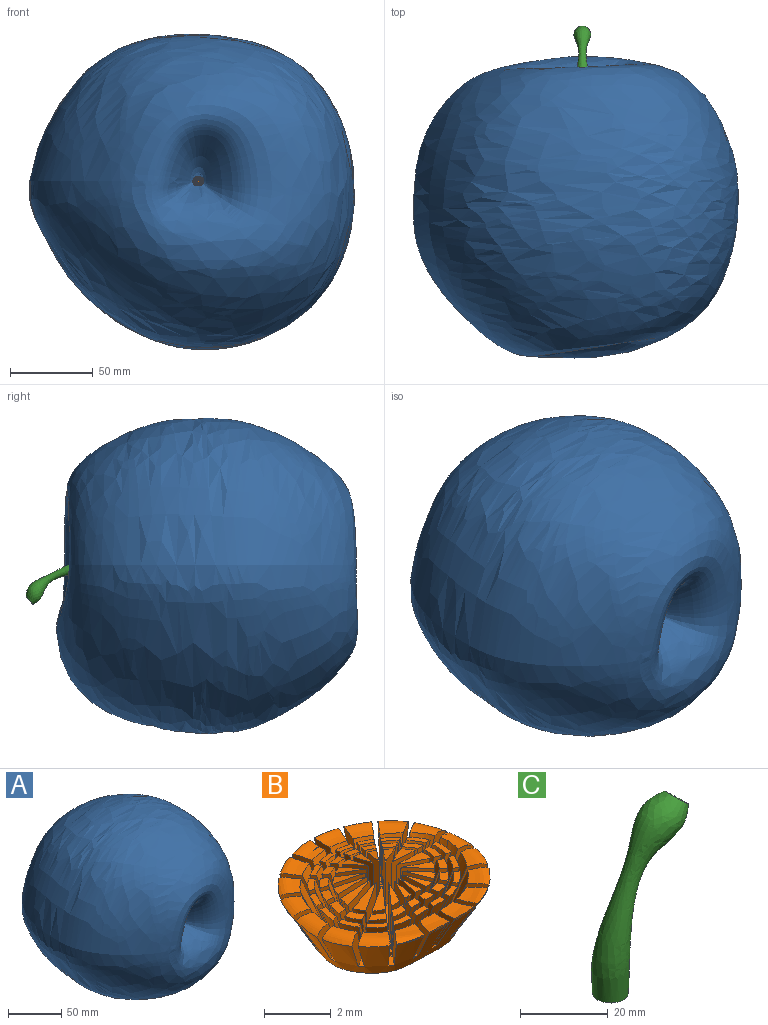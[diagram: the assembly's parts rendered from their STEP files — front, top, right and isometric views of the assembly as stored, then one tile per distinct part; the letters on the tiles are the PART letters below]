
ASSEMBLY  parts=3 mates=2
PART A: 3 faces, bbox 196.9x182.4x190.9 mm
  f0: plane 5.17x4.24mm, normal (0,-1,0), area 15.4mm2, adj f2
  f1: plane 5.17x4.24mm, normal (0,1,0), area 15.4mm2, adj f2
  f2: bspline ~196.63x190.63mm, area 122945.4mm2, adj f0,f1
PART B: 333 faces, bbox 7.9x6.9x3.2 mm
  f0: plane 0.16x0.05mm, normal (0,0,1), area 0mm2, adj f23,f253,f268
  f1: plane 0.15x0.1mm, normal (0,0,1), area 0mm2, adj f22,f260,f261
  f2: plane 0.15x0.1mm, normal (0,0,1), area 0mm2, adj f27,f245,f276
  f3: plane 0.13x0.12mm, normal (0,0,1), area 0mm2, adj f26,f252,f269
  f4: plane 0.13x0.12mm, normal (0,0,1), area 0mm2, adj f30,f237,f284
  f5: plane 0.15x0.08mm, normal (0,0,1), area 0mm2, adj f29,f244,f277
  f6: plane 0.15x0.08mm, normal (0,0,1), area 0mm2, adj f32,f229,f292
  f7: plane 0.15x0.05mm, normal (0,0,1), area 0mm2, adj f31,f236,f285
  f8: plane 0.15x0.05mm, normal (0,0,1), area 0mm2, adj f35,f221,f300
  f9: plane 0.15x0.08mm, normal (0,0,1), area 0mm2, adj f34,f228,f293
  f10: plane 0.15x0.08mm, normal (0,0,1), area 0mm2, adj f39,f213,f308
  f11: plane 0.13x0.12mm, normal (0,0,1), area 0mm2, adj f38,f220,f301
  f12: plane 0.13x0.12mm, normal (0,0,1), area 0mm2, adj f43,f205,f316
  f13: plane 0.15x0.1mm, normal (0,0,1), area 0mm2, adj f42,f212,f309
  f14: plane 0.15x0.1mm, normal (0,0,1), area 0mm2, adj f47,f197,f324
  f15: plane 0.16x0.05mm, normal (0,0,1), area 0mm2, adj f46,f204,f317
  f16: plane 0.16x0.05mm, normal (0,0,1), area 0mm2, adj f50,f190,f328
  f17: plane 0.16x0.05mm, normal (0,0,1), area 0mm2, adj f51,f177,f332
  f18: bspline ~2.16x0.71mm, area 0.1mm2, adj f75,f259,f262
  f19: bspline ~0.87x0.23mm, area 0.1mm2, adj f76,f253,f268
  f20: bspline ~1.79x1.22mm, area 0.1mm2, adj f53,f176,f254,f267
  f21: bspline ~1.67x0.54mm, area 0.1mm2, adj f49,f54,f255,f266
  f22: plane 1.67x0.7mm, normal (0.77,-0.64,0), area 1.1mm2, adj f1,f74,f80,f260,f261
  f23: plane 1.67x0.73mm, normal (1,0,0), area 0.8mm2, adj f0,f76,f80,f253,f268
  f24: bspline ~1.83x1.04mm, area 0.1mm2, adj f54,f186,f247,f274
  f25: bspline ~1.95x1.66mm, area 0mm2, adj f53,f163,f246,f275
  f26: plane 1.68x0.9mm, normal (0.5,-0.87,0), area 1.3mm2, adj f3,f74,f80,f252,f269
  f27: plane 1.67x0.78mm, normal (0.94,-0.34,0), area 1mm2, adj f2,f79,f80,f245,f276
  f28: bspline ~0.84x0.77mm, area 0mm2, adj f54,f173,f282
  f29: plane 1.69x1.26mm, normal (0.17,-0.98,0), area 1.6mm2, adj f5,f74,f80,f244,f277
  f30: plane 1.68x0.84mm, normal (0.77,-0.64,0), area 1.3mm2, adj f4,f79,f80,f237,f284
  f31: plane 1.69x1.25mm, normal (-0.17,-0.98,0), area 1.6mm2, adj f7,f76,f80,f236,f285
  f32: plane 1.69x1.07mm, normal (0.5,-0.87,0), area 1.6mm2, adj f6,f79,f80,f229,f292
  f33: bspline ~0.64x0.63mm, area 0mm2, adj f55,f125,f298
  f34: plane 1.69x0.96mm, normal (-0.5,-0.87,0), area 1.4mm2, adj f9,f76,f80,f228,f293
  f35: plane 1.69x1.23mm, normal (0.17,-0.98,0), area 1.6mm2, adj f8,f79,f80,f221,f300
  f36: bspline ~2.43x1.36mm, area 0mm2, adj f53,f214,f307
  f37: bspline ~1.58x1.45mm, area 0mm2, adj f55,f113,f215,f306
  f38: plane 1.68x0.77mm, normal (-0.77,-0.64,0), area 1.2mm2, adj f11,f76,f80,f220,f301
  f39: plane 1.69x1.1mm, normal (-0.17,-0.98,0), area 1.4mm2, adj f10,f74,f80,f213,f308
  f40: bspline ~1.64x1.62mm, area 0mm2, adj f53,f128,f206,f315
  f41: bspline ~1.89x1.15mm, area 0.1mm2, adj f55,f101,f207,f314
  f42: plane 1.67x0.8mm, normal (-0.94,-0.34,0), area 1mm2, adj f13,f76,f80,f212,f309
  f43: plane 1.68x0.91mm, normal (-0.5,-0.87,0), area 1.3mm2, adj f12,f74,f80,f205,f316
  f44: bspline ~1.92x1.22mm, area 0.1mm2, adj f53,f115,f198,f323
  f45: bspline ~1.91x0.6mm, area 0.1mm2, adj f55,f89,f199,f322
  f46: plane 1.67x0.74mm, normal (-1,0,0), area 0.9mm2, adj f15,f76,f80,f204,f317
  f47: plane 1.68x0.74mm, normal (-0.77,-0.64,0), area 1.2mm2, adj f14,f74,f80,f197,f324
  f48: bspline ~2.16x0.74mm, area 0.1mm2, adj f53,f104,f191,f327
  f49: bspline ~1.3x0.48mm, area 0mm2, adj f21,f55,f192,f266
  f50: plane 1.67x0.86mm, normal (-0.94,-0.34,0), area 1.1mm2, adj f16,f74,f80,f190,f328
  f51: plane 1.67x0.88mm, normal (-1,0,0), area 1.1mm2, adj f17,f74,f80,f177,f332
  f52: bspline ~2.31x0.97mm, area 0.1mm2, adj f53,f92,f188,f329
  f53: bspline ~7.64x3.37mm, area 12.9mm2, adj f20,f25,f36,f40,f44,f48,f52,f54
  f54: bspline ~3.77x3.61mm, area 6.9mm2, adj f21,f24,f28,f53,f55,f56,f149,f150
  f55: bspline ~4.21x3.53mm, area 7.2mm2, adj f33,f37,f41,f45,f49,f53,f54,f56
  f56: plane 4.92x3.99mm, normal (0,0,-1), area 15.4mm2, adj f53,f54,f55
  f57: bspline ~5.01x2.2mm, area 7.3mm2, adj f58,f60,f63,f87,f88,f99,f100,f111
  f58: bspline ~4.2x1.8mm, area 0.9mm2, adj f57,f59,f61,f64
  f59: bspline ~5.49x2.42mm, area 8.7mm2, adj f58,f62,f65,f91,f92,f103,f104,f115
  f60: bspline ~3.4x2.79mm, area 4.1mm2, adj f57,f61,f63,f85,f86,f97,f98,f109
  f61: bspline ~2.52x1.58mm, area 0.5mm2, adj f58,f60,f62,f64
  f62: bspline ~3.51x2.78mm, area 4.9mm2, adj f59,f61,f65,f89,f90,f101,f102,f113
  f63: bspline ~2.79x2.79mm, area 3.9mm2, adj f57,f60,f64,f147,f148,f159,f160,f171
  f64: bspline ~1.79x1.74mm, area 0.4mm2, adj f58,f61,f63,f65
  f65: bspline ~2.94x2.81mm, area 4.7mm2, adj f59,f62,f64,f149,f150,f161,f162,f173
  f66: bspline ~2.09x1.91mm, area 3.3mm2, adj f68,f70,f71,f147,f148,f159,f160,f171
  f67: bspline ~1.9x1.74mm, area 3mm2, adj f69,f71,f72,f141,f142,f153,f154,f165
  f68: bspline ~5.06x2.19mm, area 6.5mm2, adj f66,f70,f71,f87,f88,f99,f100,f111
  f69: bspline ~4.83x2.38mm, area 5.9mm2, adj f67,f71,f72,f83,f84,f95,f96,f107
  f70: bspline ~2.72x1.91mm, area 3.7mm2, adj f66,f68,f71,f85,f86,f97,f98,f109
  f71: plane 3.83x2.88mm, normal (0,0,1), area 1.1mm2, adj f66,f67,f68,f69,f70,f72
  f72: bspline ~2.58x1.72mm, area 3.4mm2, adj f67,f69,f71,f81,f82,f93,f94,f105
  f73: bspline ~3.84x1.56mm, area 4.6mm2, adj f75,f77,f78,f83,f84,f95,f96,f107
  f74: bspline ~3.54x1.59mm, area 4.2mm2, adj f22,f26,f29,f39,f43,f47,f50,f51
  f75: bspline ~2.29x1.58mm, area 2.6mm2, adj f18,f73,f77,f78,f81,f82,f93,f94
  f76: bspline ~2.16x1.61mm, area 2.4mm2, adj f19,f23,f31,f34,f38,f42,f46,f74
  f77: bspline ~1.7x1.56mm, area 2mm2, adj f73,f75,f78,f141,f142,f153,f154,f165
  f78: plane 3x2.02mm, normal (0,0,1), area 0.3mm2, adj f73,f74,f75,f76,f77,f79
  f79: bspline ~2.28x1.74mm, area 1.9mm2, adj f27,f30,f32,f35,f74,f76,f78,f80
  f80: plane 2.93x1.98mm, normal (0,0,1), area 3mm2, adj f22,f23,f26,f27,f29,f30,f31,f32
  f81: plane 1.48x0.73mm, normal (-1,0,0), area 0.4mm2, adj f72,f75,f82,f318
  f82: plane 0.32x0.2mm, normal (0,0,1), area 0.1mm2, adj f72,f75,f81,f196
  f83: plane 1.46x0.73mm, normal (-1,0,0), area 0.4mm2, adj f69,f73,f84,f331
  f84: plane 0.32x0.19mm, normal (0,0,1), area 0.1mm2, adj f69,f73,f83,f195
  f85: plane 1.4x0.65mm, normal (-1,0,0), area 0.2mm2, adj f60,f70,f86,f320
  f86: plane 0.2x0.16mm, normal (0,0,1), area 0mm2, adj f60,f70,f85,f194
  f87: plane 1.39x0.65mm, normal (-1,0,0), area 0.2mm2, adj f57,f68,f88,f330
  f88: plane 0.19x0.16mm, normal (0,0,1), area 0mm2, adj f57,f68,f87,f193
  f89: plane 1.48x1.34mm, normal (-1,0,0), area 0.8mm2, adj f45,f55,f62,f90,f322
  f90: plane 0.47x0.19mm, normal (0,0,1), area 0.1mm2, adj f55,f62,f89,f192
  f91: plane 0.46x0.19mm, normal (0,0,1), area 0.1mm2, adj f53,f59,f92,f191
  f92: plane 1.48x1.34mm, normal (-1,0,0), area 0.8mm2, adj f52,f53,f59,f91,f329
  f93: plane 1.46x0.7mm, normal (-0.94,-0.34,0), area 0.4mm2, adj f72,f75,f94,f310
  f94: plane 0.33x0.33mm, normal (0,0,1), area 0.1mm2, adj f72,f75,f93,f203
  f95: plane 1.45x0.68mm, normal (-0.94,-0.34,0), area 0.4mm2, adj f69,f73,f96,f325
  f96: plane 0.34x0.29mm, normal (0,0,1), area 0.1mm2, adj f69,f73,f95,f202
  f97: plane 1.39x0.62mm, normal (-0.94,-0.34,0), area 0.2mm2, adj f60,f70,f98,f312
  f98: plane 0.26x0.17mm, normal (0,0,1), area 0mm2, adj f60,f70,f97,f201
  f99: plane 1.38x0.61mm, normal (-0.94,-0.34,0), area 0.2mm2, adj f57,f68,f100,f326
  f100: plane 0.24x0.19mm, normal (0,0,1), area 0mm2, adj f57,f68,f99,f200
  f101: plane 1.48x1.28mm, normal (-0.94,-0.34,0), area 0.8mm2, adj f41,f55,f62,f102,f314
  f102: plane 0.47x0.36mm, normal (0,0,1), area 0.1mm2, adj f55,f62,f101,f199
  f103: plane 0.49x0.34mm, normal (0,0,1), area 0.1mm2, adj f53,f59,f104,f198
  f104: plane 1.48x1.26mm, normal (-0.94,-0.34,0), area 0.8mm2, adj f48,f53,f59,f103,f327
  f105: plane 1.44x0.56mm, normal (-0.77,-0.64,0), area 0.4mm2, adj f72,f75,f106,f302
  f106: plane 0.4x0.34mm, normal (0,0,1), area 0.1mm2, adj f72,f75,f105,f211
  f107: plane 1.44x0.56mm, normal (-0.77,-0.64,0), area 0.4mm2, adj f69,f73,f108,f319
  f108: plane 0.37x0.34mm, normal (0,0,1), area 0.1mm2, adj f69,f73,f107,f210
  f109: plane 1.37x0.5mm, normal (-0.77,-0.64,0), area 0.2mm2, adj f60,f70,f110,f304
  f110: plane 0.27x0.22mm, normal (0,0,1), area 0mm2, adj f60,f70,f109,f209
  f111: plane 1.37x0.5mm, normal (-0.77,-0.64,0), area 0.2mm2, adj f57,f68,f112,f321
  f112: plane 0.26x0.22mm, normal (0,0,1), area 0mm2, adj f57,f68,f111,f208
  f113: plane 1.45x1.02mm, normal (-0.77,-0.64,0), area 0.8mm2, adj f37,f55,f62,f114,f306
  f114: plane 0.47x0.46mm, normal (0,0,1), area 0.1mm2, adj f55,f62,f113,f207
  f115: plane 1.46x1.03mm, normal (-0.77,-0.64,0), area 0.8mm2, adj f44,f53,f59,f116,f323
  f116: plane 0.46x0.46mm, normal (0,0,1), area 0.1mm2, adj f53,f59,f115,f206
  f117: plane 1.42x0.62mm, normal (-0.5,-0.87,0), area 0.4mm2, adj f72,f75,f118,f294
  f118: plane 0.41x0.3mm, normal (0,0,1), area 0.1mm2, adj f72,f75,f117,f219
  f119: plane 1.43x0.63mm, normal (-0.5,-0.87,0), area 0.4mm2, adj f69,f73,f120,f311
  f120: plane 0.4x0.31mm, normal (0,0,1), area 0.1mm2, adj f69,f73,f119,f218
  f121: plane 1.36x0.56mm, normal (-0.5,-0.87,0), area 0.2mm2, adj f60,f70,f122,f296
  f122: plane 0.26x0.22mm, normal (0,0,1), area 0mm2, adj f60,f70,f121,f217
  f123: plane 1.36x0.56mm, normal (-0.5,-0.87,0), area 0.2mm2, adj f57,f68,f124,f313
  f124: plane 0.25x0.23mm, normal (0,0,1), area 0mm2, adj f57,f68,f123,f216
  f125: plane 1.37x1.05mm, normal (-0.5,-0.87,0), area 0.8mm2, adj f33,f55,f62,f126,f298
  f126: plane 0.53x0.38mm, normal (0,0,1), area 0.1mm2, adj f55,f62,f125,f215
  f127: plane 0.51x0.39mm, normal (0,0,1), area 0.1mm2, adj f53,f59,f128,f214
  f128: plane 1.43x1.12mm, normal (-0.5,-0.87,0), area 0.8mm2, adj f40,f53,f59,f127,f315
  f129: plane 1.39x0.71mm, normal (-0.17,-0.98,0), area 0.4mm2, adj f72,f75,f130,f287
  f130: plane 0.42x0.24mm, normal (0,0,1), area 0.1mm2, adj f72,f75,f129,f227
  f131: plane 1.41x0.71mm, normal (-0.17,-0.98,0), area 0.4mm2, adj f69,f73,f132,f303
  f132: plane 0.38x0.24mm, normal (0,0,1), area 0.1mm2, adj f69,f73,f131,f226
  f133: plane 1.35x0.63mm, normal (-0.17,-0.98,0), area 0.2mm2, adj f60,f70,f134,f288
  f134: plane 0.24x0.21mm, normal (0,0,1), area 0mm2, adj f60,f70,f133,f225
  f135: plane 1.36x0.64mm, normal (-0.17,-0.98,0), area 0.2mm2, adj f57,f68,f136,f305
  f136: plane 0.21x0.21mm, normal (0,0,1), area 0mm2, adj f57,f68,f135,f224
  f137: plane 1.4x1.16mm, normal (-0.17,-0.98,0), area 0.7mm2, adj f55,f62,f138,f291
  f138: plane 0.53x0.26mm, normal (0,0,1), area 0.1mm2, adj f55,f62,f137,f223
  f139: plane 1.4x1.22mm, normal (-0.17,-0.98,0), area 0.8mm2, adj f53,f59,f140,f307
  f140: plane 0.51x0.27mm, normal (0,0,1), area 0.1mm2, adj f53,f59,f139,f222
  f141: plane 1.4x0.73mm, normal (0.17,-0.98,0), area 0.4mm2, adj f67,f77,f142,f295
  f142: plane 0.39x0.3mm, normal (0,0,1), area 0.1mm2, adj f67,f77,f141,f235
  f143: plane 1.41x0.77mm, normal (0.17,-0.98,0), area 0.4mm2, adj f69,f73,f144,f279
  f144: plane 0.45x0.25mm, normal (0,0,1), area 0.1mm2, adj f69,f73,f143,f234
  f145: plane 1.38x0.68mm, normal (0.17,-0.98,0), area 0.2mm2, adj f57,f68,f146,f280
  f146: plane 0.23x0.22mm, normal (0,0,1), area 0mm2, adj f57,f68,f145,f233
  f147: plane 1.35x0.64mm, normal (0.17,-0.98,0), area 0.2mm2, adj f63,f66,f148,f297
  f148: plane 0.24x0.18mm, normal (0,0,1), area 0mm2, adj f63,f66,f147,f232
  f149: plane 1.4x1.17mm, normal (0.17,-0.98,0), area 0.7mm2, adj f54,f65,f150,f299
  f150: plane 0.47x0.28mm, normal (0,0,1), area 0.1mm2, adj f54,f65,f149,f231
  f151: plane 0.52x0.27mm, normal (0,0,1), area 0.1mm2, adj f53,f59,f152,f230
  f152: plane 1.41x1.17mm, normal (0.17,-0.98,0), area 0.8mm2, adj f53,f59,f151,f283
  f153: plane 1.42x0.64mm, normal (0.5,-0.87,0), area 0.4mm2, adj f67,f77,f154,f286
  f154: plane 0.43x0.34mm, normal (0,0,1), area 0.1mm2, adj f67,f77,f153,f243
  f155: plane 1.44x0.68mm, normal (0.5,-0.87,0), area 0.4mm2, adj f69,f73,f156,f271
  f156: plane 0.45x0.29mm, normal (0,0,1), area 0.1mm2, adj f69,f73,f155,f242
  f157: plane 1.38x0.6mm, normal (0.5,-0.87,0), area 0.2mm2, adj f57,f68,f158,f272
  f158: plane 0.29x0.21mm, normal (0,0,1), area 0mm2, adj f57,f68,f157,f241
  f159: plane 1.36x0.57mm, normal (0.5,-0.87,0), area 0.2mm2, adj f63,f66,f160,f289
  f160: plane 0.25x0.23mm, normal (0,0,1), area 0mm2, adj f63,f66,f159,f240
  f161: plane 1.39x1.03mm, normal (0.5,-0.87,0), area 0.7mm2, adj f54,f65,f162,f290
  f162: plane 0.52x0.38mm, normal (0,0,1), area 0.1mm2, adj f54,f65,f161,f239
  f163: plane 1.42x1.14mm, normal (0.5,-0.87,0), area 0.8mm2, adj f25,f53,f59,f164,f275
  f164: plane 0.56x0.38mm, normal (0,0,1), area 0.1mm2, adj f53,f59,f163,f238
  f165: plane 1.45x0.61mm, normal (0.77,-0.64,0), area 0.4mm2, adj f67,f77,f166,f278
  f166: plane 0.48x0.34mm, normal (0,0,1), area 0.1mm2, adj f67,f77,f165,f251
  f167: plane 1.47x0.58mm, normal (0.77,-0.64,0), area 0.4mm2, adj f69,f73,f168,f263
  f168: plane 0.37x0.34mm, normal (0,0,1), area 0.1mm2, adj f69,f73,f167,f250
  f169: plane 1.39x0.51mm, normal (0.77,-0.64,0), area 0.2mm2, adj f57,f68,f170,f264
  f170: plane 0.26x0.21mm, normal (0,0,1), area 0mm2, adj f57,f68,f169,f249
  f171: plane 1.39x0.54mm, normal (0.77,-0.64,0), area 0.2mm2, adj f63,f66,f172,f281
  f172: plane 0.32x0.2mm, normal (0,0,1), area 0mm2, adj f63,f66,f171,f248
  f173: plane 1.41x0.97mm, normal (0.77,-0.64,0), area 0.8mm2, adj f28,f54,f65,f174,f282
  f174: plane 0.49x0.45mm, normal (0,0,1), area 0.1mm2, adj f54,f65,f173,f247
  f175: plane 0.46x0.46mm, normal (0,0,1), area 0.1mm2, adj f53,f59,f176,f246
  f176: plane 1.48x1.06mm, normal (0.77,-0.64,0), area 0.8mm2, adj f20,f53,f59,f175,f267
  f177: plane 1.67x0.82mm, normal (0.94,-0.34,0), area 1.1mm2, adj f17,f51,f74,f80,f332
  f178: plane 1.47x0.73mm, normal (0.94,-0.34,0), area 0.4mm2, adj f67,f77,f179,f270
  f179: plane 0.32x0.31mm, normal (0,0,1), area 0.1mm2, adj f67,f75,f77,f178,f259
  f180: plane 1.48x0.69mm, normal (0.94,-0.34,0), area 0.4mm2, adj f69,f73,f181,f331
  f181: plane 0.36x0.29mm, normal (0,0,1), area 0.1mm2, adj f69,f73,f180,f258
  f182: plane 1.4x0.62mm, normal (0.94,-0.34,0), area 0.2mm2, adj f57,f68,f183,f330
  f183: plane 0.23x0.21mm, normal (0,0,1), area 0mm2, adj f57,f68,f182,f257
  f184: plane 1.39x0.64mm, normal (0.94,-0.34,0), area 0.2mm2, adj f63,f66,f185,f273
  f185: plane 0.26x0.16mm, normal (0,0,1), area 0mm2, adj f63,f66,f184,f256
  f186: plane 1.49x1.31mm, normal (0.94,-0.34,0), area 0.8mm2, adj f24,f54,f65,f187,f274
  f187: plane 0.46x0.36mm, normal (0,0,1), area 0.1mm2, adj f54,f65,f186,f255
  f188: plane 1.48x1.27mm, normal (0.94,-0.34,0), area 0.8mm2, adj f52,f53,f59,f189,f329
  f189: plane 0.5x0.34mm, normal (0,0,1), area 0.1mm2, adj f53,f59,f188,f254
  f190: plane 1.67x0.89mm, normal (1,0,0), area 1.1mm2, adj f16,f50,f74,f80,f328
  f191: plane 1.48x1.34mm, normal (1,0,0), area 0.8mm2, adj f48,f53,f59,f91,f327
  f192: plane 1.47x1.33mm, normal (1,0,0), area 0.8mm2, adj f49,f55,f62,f90,f266
  f193: plane 1.39x0.65mm, normal (1,0,0), area 0.2mm2, adj f57,f68,f88,f326
  f194: plane 1.4x0.66mm, normal (1,0,0), area 0.2mm2, adj f60,f70,f86,f265
  f195: plane 1.47x0.73mm, normal (1,0,0), area 0.4mm2, adj f69,f73,f84,f325
  f196: plane 1.48x0.73mm, normal (1,0,0), area 0.4mm2, adj f72,f75,f82,f262
  f197: plane 1.68x0.87mm, normal (0.94,0.34,0), area 1.1mm2, adj f14,f47,f74,f80,f324
  f198: plane 1.47x1.26mm, normal (0.94,0.34,0), area 0.8mm2, adj f44,f53,f59,f103,f323
  f199: plane 1.49x1.31mm, normal (0.94,0.34,0), area 0.8mm2, adj f45,f55,f62,f102,f322
  f200: plane 1.38x0.61mm, normal (0.94,0.34,0), area 0.2mm2, adj f57,f68,f100,f321
  f201: plane 1.39x0.63mm, normal (0.94,0.34,0), area 0.2mm2, adj f60,f70,f98,f320
  f202: plane 1.46x0.68mm, normal (0.94,0.34,0), area 0.4mm2, adj f69,f73,f96,f319
  f203: plane 1.47x0.72mm, normal (0.94,0.34,0), area 0.4mm2, adj f72,f75,f94,f318
  f204: plane 1.67x0.74mm, normal (0.94,0.34,0), area 0.9mm2, adj f15,f46,f76,f80,f317
  f205: plane 1.68x0.77mm, normal (0.77,0.64,0), area 1.2mm2, adj f12,f43,f74,f80,f316
  f206: plane 1.45x1.02mm, normal (0.77,0.64,0), area 0.8mm2, adj f40,f53,f59,f116,f315
  f207: plane 1.46x1.04mm, normal (0.77,0.64,0), area 0.8mm2, adj f41,f55,f62,f114,f314
  f208: plane 1.38x0.5mm, normal (0.77,0.64,0), area 0.2mm2, adj f57,f68,f112,f313
  f209: plane 1.37x0.5mm, normal (0.77,0.64,0), area 0.2mm2, adj f60,f70,f110,f312
  f210: plane 1.44x0.56mm, normal (0.77,0.64,0), area 0.4mm2, adj f69,f73,f108,f311
  f211: plane 1.45x0.58mm, normal (0.77,0.64,0), area 0.4mm2, adj f72,f75,f106,f310
  f212: plane 1.68x0.73mm, normal (0.77,0.64,0), area 1.2mm2, adj f13,f42,f76,f80,f309
  f213: plane 1.68x0.93mm, normal (0.5,0.87,0), area 1.4mm2, adj f10,f39,f74,f80,f308
  f214: plane 1.43x1.1mm, normal (0.5,0.87,0), area 0.8mm2, adj f36,f53,f59,f127,f307
  f215: plane 1.42x1.11mm, normal (0.5,0.87,0), area 0.8mm2, adj f37,f55,f62,f126,f306
  f216: plane 1.37x0.56mm, normal (0.5,0.87,0), area 0.2mm2, adj f57,f68,f124,f305
  f217: plane 1.36x0.57mm, normal (0.5,0.87,0), area 0.2mm2, adj f60,f70,f122,f304
  f218: plane 1.43x0.63mm, normal (0.5,0.87,0), area 0.4mm2, adj f69,f73,f120,f303
  f219: plane 1.42x0.64mm, normal (0.5,0.87,0), area 0.4mm2, adj f72,f75,f118,f302
  f220: plane 1.68x0.93mm, normal (0.5,0.87,0), area 1.3mm2, adj f11,f38,f76,f80,f301
  f221: plane 1.69x1.13mm, normal (0.17,0.98,0), area 1.5mm2, adj f8,f35,f74,f80,f300
  f222: plane 1.4x1.2mm, normal (0.17,0.98,0), area 0.8mm2, adj f53,f59,f140,f299
  f223: plane 1.39x1.18mm, normal (0.17,0.98,0), area 0.8mm2, adj f55,f62,f138,f298
  f224: plane 1.35x0.63mm, normal (0.17,0.98,0), area 0.2mm2, adj f57,f68,f136,f297
  f225: plane 1.35x0.65mm, normal (0.17,0.98,0), area 0.2mm2, adj f60,f70,f134,f296
  f226: plane 1.41x0.7mm, normal (0.17,0.98,0), area 0.4mm2, adj f69,f73,f132,f295
  f227: plane 1.4x0.73mm, normal (0.17,0.98,0), area 0.4mm2, adj f72,f75,f130,f294
  f228: plane 1.69x1.2mm, normal (0.17,0.98,0), area 1.5mm2, adj f9,f34,f76,f80,f293
  f229: plane 1.7x1.27mm, normal (-0.17,0.98,0), area 1.7mm2, adj f6,f32,f79,f80,f292
  f230: plane 1.4x1.15mm, normal (-0.17,0.98,0), area 0.7mm2, adj f53,f59,f151,f291
  f231: plane 1.4x1.15mm, normal (-0.17,0.98,0), area 0.7mm2, adj f54,f65,f150,f290
  f232: plane 1.37x0.64mm, normal (-0.17,0.98,0), area 0.2mm2, adj f63,f66,f148,f289
  f233: plane 1.37x0.64mm, normal (-0.17,0.98,0), area 0.2mm2, adj f57,f68,f146,f288
  f234: plane 1.43x0.73mm, normal (-0.17,0.98,0), area 0.4mm2, adj f69,f73,f144,f287
  f235: plane 1.42x0.71mm, normal (-0.17,0.98,0), area 0.4mm2, adj f67,f77,f142,f286
  f236: plane 1.7x1.31mm, normal (-0.17,0.98,0), area 1.7mm2, adj f7,f31,f74,f80,f285
  f237: plane 1.69x1.04mm, normal (-0.5,0.87,0), area 1.5mm2, adj f4,f30,f79,f80,f284
  f238: plane 1.4x1.09mm, normal (-0.5,0.87,0), area 0.8mm2, adj f53,f59,f164,f283
  f239: plane 1.39x1.04mm, normal (-0.5,0.87,0), area 0.8mm2, adj f54,f65,f162,f282
  f240: plane 1.37x0.58mm, normal (-0.5,0.87,0), area 0.2mm2, adj f63,f66,f160,f281
  f241: plane 1.37x0.59mm, normal (-0.5,0.87,0), area 0.2mm2, adj f57,f68,f158,f280
  f242: plane 1.42x0.66mm, normal (-0.5,0.87,0), area 0.4mm2, adj f69,f73,f156,f279
  f243: plane 1.49x0.72mm, normal (-0.5,0.87,0), area 0.4mm2, adj f67,f77,f154,f278
  f244: plane 1.69x0.96mm, normal (-0.5,0.87,0), area 1.4mm2, adj f5,f29,f74,f80,f277
  f245: plane 1.68x0.77mm, normal (-0.77,0.64,0), area 1.2mm2, adj f2,f27,f79,f80,f276
  f246: plane 1.47x1.04mm, normal (-0.77,0.64,0), area 0.8mm2, adj f25,f53,f59,f175,f275
  f247: plane 1.43x1.02mm, normal (-0.77,0.64,0), area 0.8mm2, adj f24,f54,f65,f174,f274
  f248: plane 1.4x0.57mm, normal (-0.77,0.64,0), area 0.3mm2, adj f63,f66,f172,f273
  f249: plane 1.39x0.51mm, normal (-0.77,0.64,0), area 0.2mm2, adj f57,f68,f170,f272
  f250: plane 1.46x0.57mm, normal (-0.77,0.64,0), area 0.4mm2, adj f69,f73,f168,f271
  f251: plane 1.46x0.67mm, normal (-0.77,0.64,0), area 0.5mm2, adj f67,f77,f166,f270
  f252: plane 1.68x0.72mm, normal (-0.77,0.64,0), area 1.1mm2, adj f3,f26,f74,f80,f269
  f253: plane 1.67x0.72mm, normal (-0.94,0.34,0), area 0.9mm2, adj f0,f19,f23,f76,f80,f268
  f254: plane 1.48x1.27mm, normal (-0.94,0.34,0), area 0.8mm2, adj f20,f53,f59,f189,f267
  f255: plane 1.49x1.33mm, normal (-0.94,0.34,0), area 0.8mm2, adj f21,f54,f65,f187,f266
  f256: plane 1.4x0.65mm, normal (-0.94,0.34,0), area 0.3mm2, adj f63,f66,f185,f265
  f257: plane 1.39x0.61mm, normal (-0.94,0.34,0), area 0.2mm2, adj f57,f68,f183,f264
  f258: plane 1.46x0.68mm, normal (-0.94,0.34,0), area 0.4mm2, adj f69,f73,f181,f263
  f259: plane 1.48x0.73mm, normal (-0.94,0.34,0), area 0.4mm2, adj f18,f67,f75,f179,f262
  f260: plane 1.67x0.82mm, normal (-0.94,0.34,0), area 1.1mm2, adj f1,f22,f74,f80,f261
  f261: revolved ~0.73x0.55mm, area 0.1mm2, adj f1,f22,f74,f260
  f262: revolved ~0.41x0.36mm, area 0.1mm2, adj f18,f67,f72,f75,f196,f259
  f263: revolved ~0.49x0.45mm, area 0.1mm2, adj f69,f73,f167,f258
  f264: revolved ~0.58x0.46mm, area 0.1mm2, adj f57,f68,f169,f257
  f265: revolved ~0.54x0.35mm, area 0.1mm2, adj f60,f63,f66,f70,f194,f256
  f266: revolved ~0.88x0.87mm, area 0.5mm2, adj f21,f49,f62,f65,f192,f255
  f267: revolved ~1.03x1mm, area 0.5mm2, adj f20,f59,f176,f254
  f268: revolved ~0.61x0.3mm, area 0.1mm2, adj f0,f19,f23,f76,f253
  f269: revolved ~0.8x0.72mm, area 0.1mm2, adj f3,f26,f74,f252
  f270: revolved ~0.59x0.59mm, area 0.1mm2, adj f67,f77,f178,f251
  f271: revolved ~0.58x0.57mm, area 0.1mm2, adj f69,f73,f155,f250
  f272: revolved ~0.65x0.62mm, area 0.1mm2, adj f57,f68,f157,f249
  f273: revolved ~0.67x0.61mm, area 0.1mm2, adj f63,f66,f184,f248
  f274: revolved ~1.13x1.12mm, area 0.5mm2, adj f24,f65,f186,f247
  f275: revolved ~1.14x1.14mm, area 0.5mm2, adj f25,f59,f163,f246
  f276: revolved ~0.8x0.6mm, area 0.1mm2, adj f2,f27,f79,f245
  f277: revolved ~1.1x0.63mm, area 0.2mm2, adj f5,f29,f74,f244
  f278: revolved ~0.61x0.59mm, area 0.1mm2, adj f67,f77,f165,f243
  f279: revolved ~0.63x0.58mm, area 0.1mm2, adj f69,f73,f143,f242
  f280: revolved ~0.72x0.55mm, area 0.1mm2, adj f57,f68,f145,f241
  f281: revolved ~0.67x0.62mm, area 0.1mm2, adj f63,f66,f171,f240
  f282: revolved ~1.11x1.1mm, area 0.6mm2, adj f28,f54,f65,f173,f239
  f283: revolved ~1.07x0.99mm, area 0.6mm2, adj f53,f59,f152,f238
  f284: revolved ~0.94x0.85mm, area 0.2mm2, adj f4,f30,f79,f237
  f285: revolved ~1.13x0.44mm, area 0.2mm2, adj f7,f31,f74,f76,f236
  f286: revolved ~0.6x0.47mm, area 0.1mm2, adj f67,f77,f153,f235
  f287: revolved ~0.58x0.33mm, area 0.1mm2, adj f69,f72,f73,f75,f129,f234
  f288: revolved ~0.7x0.26mm, area 0.1mm2, adj f57,f60,f68,f70,f133,f233
  f289: revolved ~0.7x0.45mm, area 0.1mm2, adj f63,f66,f159,f232
  f290: revolved ~1.05x0.89mm, area 0.6mm2, adj f54,f65,f161,f231
  f291: revolved ~0.99x0.64mm, area 0.6mm2, adj f53,f55,f59,f62,f137,f230
  f292: revolved ~1.11x0.65mm, area 0.2mm2, adj f6,f32,f79,f229
  f293: revolved ~1.04x0.61mm, area 0.2mm2, adj f9,f34,f76,f228
  f294: revolved ~0.59x0.52mm, area 0.1mm2, adj f72,f75,f117,f227
  f295: revolved ~0.56x0.38mm, area 0.1mm2, adj f67,f69,f73,f77,f141,f226
  f296: revolved ~0.7x0.51mm, area 0.1mm2, adj f60,f70,f121,f225
  f297: revolved ~0.68x0.33mm, area 0.1mm2, adj f57,f63,f66,f68,f147,f224
  f298: revolved ~1.06x0.98mm, area 0.6mm2, adj f33,f55,f62,f125,f223
  f299: revolved ~0.98x0.74mm, area 0.6mm2, adj f53,f54,f59,f65,f149,f222
  f300: revolved ~1.05x0.41mm, area 0.2mm2, adj f8,f35,f74,f79,f221
  f301: revolved ~0.83x0.75mm, area 0.2mm2, adj f11,f38,f76,f220
  f302: revolved ~0.56x0.54mm, area 0.1mm2, adj f72,f75,f105,f219
  f303: revolved ~0.55x0.45mm, area 0.1mm2, adj f69,f73,f131,f218
  f304: revolved ~0.62x0.58mm, area 0.1mm2, adj f60,f70,f109,f217
  f305: revolved ~0.65x0.43mm, area 0.1mm2, adj f57,f68,f135,f216
  f306: revolved ~1.1x1.09mm, area 0.5mm2, adj f37,f62,f113,f215
  f307: revolved ~1.03x0.93mm, area 0.5mm2, adj f36,f53,f59,f139,f214
  f308: revolved ~0.95x0.56mm, area 0.2mm2, adj f10,f39,f74,f213
  f309: revolved ~0.77x0.58mm, area 0.1mm2, adj f13,f42,f76,f212
  f310: revolved ~0.54x0.51mm, area 0.1mm2, adj f72,f75,f93,f211
  f311: revolved ~0.55x0.53mm, area 0.1mm2, adj f69,f73,f119,f210
  f312: revolved ~0.62x0.52mm, area 0.1mm2, adj f60,f70,f97,f209
  f313: revolved ~0.61x0.56mm, area 0.1mm2, adj f57,f68,f123,f208
  f314: revolved ~1.06x1.05mm, area 0.5mm2, adj f41,f62,f101,f207
  f315: revolved ~1.09x1.07mm, area 0.5mm2, adj f40,f59,f128,f206
  f316: revolved ~0.81x0.74mm, area 0.2mm2, adj f12,f43,f74,f205
  f317: revolved ~0.64x0.31mm, area 0.1mm2, adj f15,f46,f76,f204
  f318: revolved ~0.42x0.38mm, area 0.1mm2, adj f72,f75,f81,f203
  f319: revolved ~0.52x0.47mm, area 0.1mm2, adj f69,f73,f107,f202
  f320: revolved ~0.54x0.35mm, area 0.1mm2, adj f60,f70,f85,f201
  f321: revolved ~0.6x0.48mm, area 0.1mm2, adj f57,f68,f111,f200
  f322: revolved ~0.88x0.87mm, area 0.5mm2, adj f45,f62,f89,f199
  f323: revolved ~1.04x1.01mm, area 0.5mm2, adj f44,f59,f115,f198
  f324: revolved ~0.78x0.59mm, area 0.1mm2, adj f14,f47,f74,f197
  f325: revolved ~0.45x0.34mm, area 0.1mm2, adj f69,f73,f95,f195
  f326: revolved ~0.57x0.3mm, area 0.1mm2, adj f57,f68,f99,f193
  f327: revolved ~0.89x0.81mm, area 0.5mm2, adj f48,f59,f104,f191
  f328: revolved ~0.75x0.35mm, area 0.1mm2, adj f16,f50,f74,f190
  f329: revolved ~0.88x0.8mm, area 0.5mm2, adj f52,f59,f92,f188
  f330: revolved ~0.56x0.29mm, area 0.1mm2, adj f57,f68,f87,f182
  f331: revolved ~0.44x0.33mm, area 0.1mm2, adj f69,f73,f83,f180
  f332: revolved ~0.72x0.34mm, area 0.1mm2, adj f17,f51,f74,f177
PART C: 3 faces, bbox 28.5x13x45.8 mm
  f0: plane 8.15x8.15mm, normal (0,0,-1), area 52.1mm2, adj f2
  f1: plane 6.27x4.59mm, normal (0.68,0,0.73), area 30.9mm2, adj f2
  f2: bspline ~45.8x28.5mm, area 1178.2mm2, adj f0,f1
PLACE A t=(-35.66,-41.78,25.33)mm
PLACE B rot(axis=(1,0,0),90deg) t=(-35.44,-67.18,25.22)mm
PLACE C rot(axis=(-0.58,0.58,0.58),120deg) t=(-35.44,53.22,25.22)mm
MATE fastened C.f0 <-> A.f1  axis (0,-1,0) through (-35.44,53.22,25.22)mm
MATE fastened B.f56 <-> A.f0  axis (0,1,0) through (-35.44,-67.18,25.22)mm
